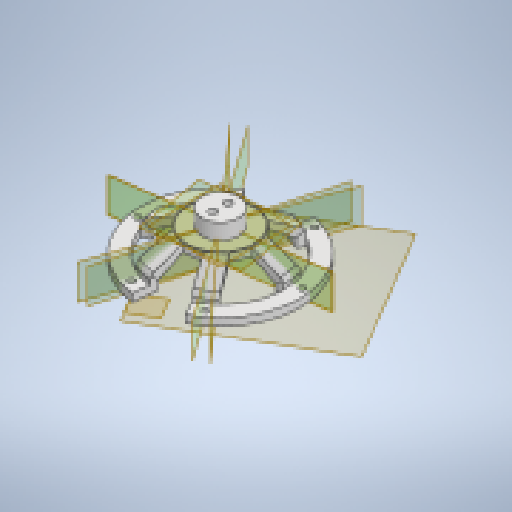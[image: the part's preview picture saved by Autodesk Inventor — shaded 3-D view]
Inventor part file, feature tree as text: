
AUTODESK INVENTOR PART (.ipt)
format: ipt  version: 2023.1 (Build 271208000, 208)  size: 569,344 bytes
history: native  units: in
note: dims shown in document units (in); Inventor stores cm internally (conversion verified against a paired STEP export)
features: other x17, plane x11, sketch x7, extrude x7, loft x6, fillet x1
ambient origin geometry x8: Origin, YZ Plane, XZ Plane, XY Plane, X Axis, Y Axis, Z Axis, Center Point
bodies: Body1 (feature_tree)
feature tree (49):
  plane  "Work Plane2"
  sketch  "Sketch2"  dims[d4=0.1575in d5=0.0in d6=0.1575in d7=0.0in]
  plane  "Work Plane3"
  extrude  "Extrusion3"  Depth=0.1575in TaperAngle=0.0deg
  extrude  "Extrusion4"  [1 undecoded]
  extrude  "Extrusion5"  [1 undecoded]
  plane  "Work Plane4"
  plane  "Work Plane5"
  plane  "Work Plane6"
  plane  "Work Plane7"
  plane  "Work Plane9"
  plane  "Work Plane10"
  plane  "Work Plane11"
  plane  "Work Plane12"
  sketch  "Sketch7"  dims[d41=0.1575in d42=0.0in d43=0.0in d44=90.0deg]
  extrude  "Extrusion7"  TaperAngle=0.0deg  [1 undecoded]
  plane  "Work Plane13"
  sketch  "Sketch10"  dims[d49=0.0in d50=90.0deg d51=0.0in d52=90.0deg]
  extrude  "Extrusion8"  TaperAngle=0.0deg  [1 undecoded]
  loft  "Loft2"
  loft  "Loft3"
  loft  "Loft4"
  loft  "Loft5"
  loft  "Loft6"
  loft  "Loft7"
  fillet  "Fillet1"  [1 undecoded]
  extrude  "Extrusion9"  Depth=0.1575in
  extrude  "Extrusion10"  Depth=0.3228in TaperAngle=0.0deg
  sketch  "Sketch3"  dims[d9=0.1575in d10=0.1575in d11=0.0in d12=0.0in d13=-0.6875in]
  sketch  "Sketch4"  dims[d38=0.22in d39=-0.3436in d40=-0.0004in]
  sketch  "Sketch9"  dims[d45=0.0in d46=90.0deg d47=0.0in d48=90.0deg]
  other  "Edges3"
  other  "Edges4"
  other  "Edges5"
  other  "Edges6"
  other  "Edges7"
  other  "Edges8"
  other  "Edges9"
  other  "Edges10"
  other  "Edges11"
  other  "Edges12"
  other  "Edges13"
  other  "Edges14"
  sketch  "Sketch11"  dims[d53=0.0in d54=90.0deg d55=0.0in d56=90.0deg d57=0.0in d58=90.0deg d59=0.0in d60=90.0deg d61=0.0in d62=90.0deg d63=0.0in d64=90.0deg d65=0.0in d66=90.0deg d67=0.1181in d68=0.3228in d69=0.0in d70=0.1654in d71=0.1654in d72=0.3228in d73=0.0in d74=0.1575in d75=0.0in d14=0.0344in d15=0.0197in d16=0.0344in]
  other  "G:\Assembly1.iam"
  other  "Assembly1.iam"
  other  "Worm Gears:1"
  other  "Worm Gear:1"
  other  "Frame:1"
note: 5 required parameter values undecoded (feature->parameter linkage not recoverable at this tier; creation-order binding heuristic only, values carry confidence <= 0.55)
